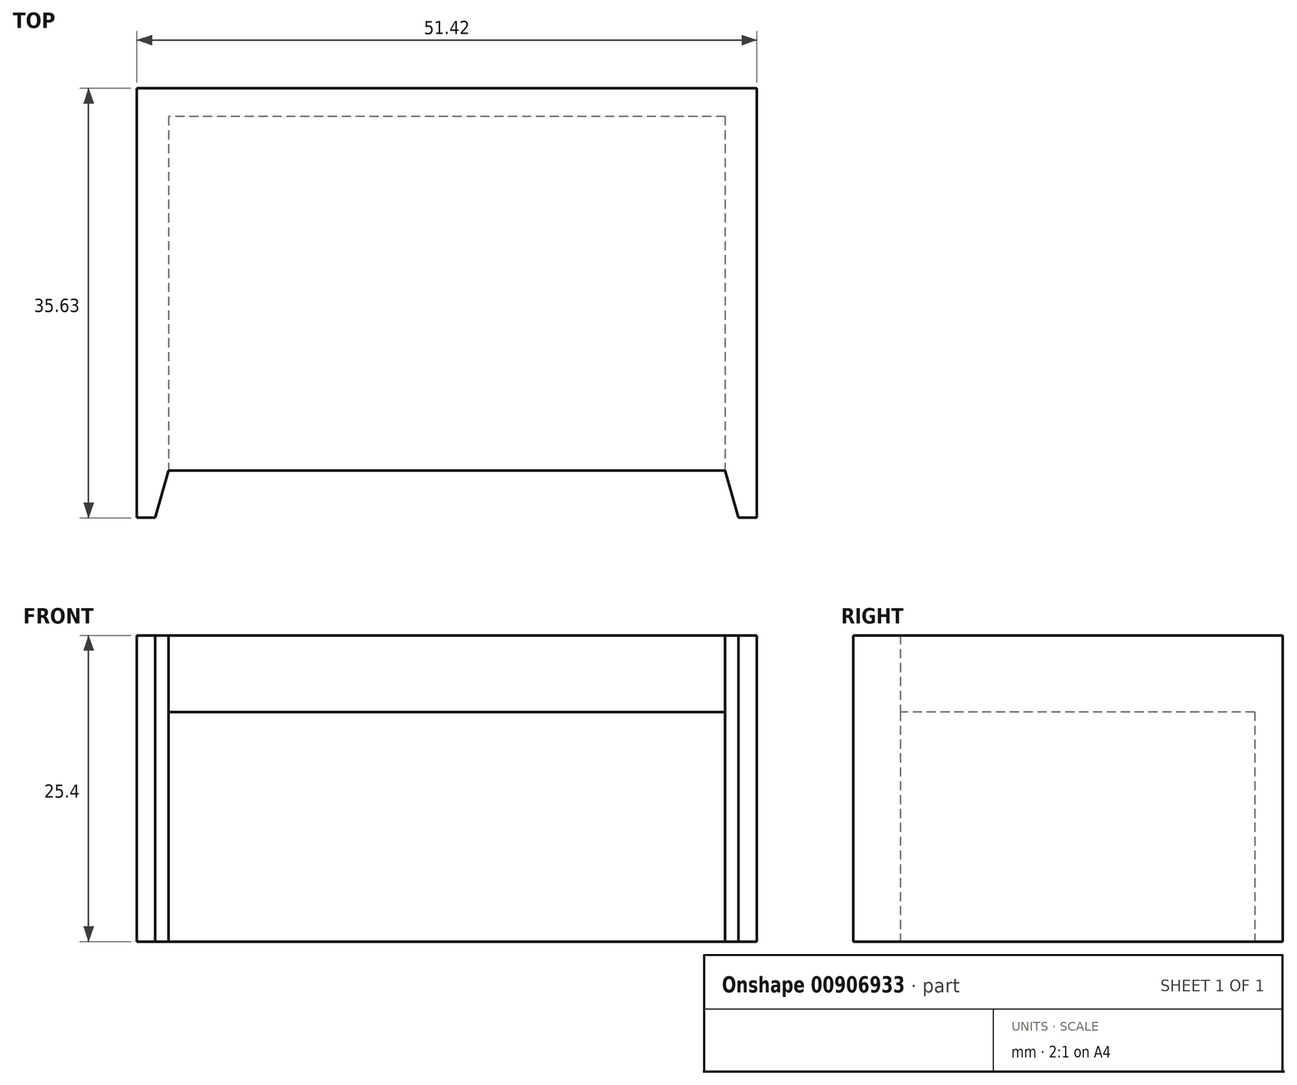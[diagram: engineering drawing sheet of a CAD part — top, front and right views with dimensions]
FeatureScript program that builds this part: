
annotation { "Feature Type Name" : "Feature", "Feature Type Description" : "" }
export const myFeature = defineFeature(function(context is Context, id is Id, definition is map)
    precondition{}
    {
        {
            var Q0;
            Q0=qCreatedBy(makeId("Top.planeOp"),FACE);
            var sketch = newSketch(context, id + "F0", { "sketchPlane" : qUnion([Q0])});
            skLineSegment(sketch, "E0.bottom", {"start": v(19.14, 62.7) * mm, "end": v(70.56, 62.7) * mm});
            skLineSegment(sketch, "E0.top", {"start": v(19.14, 31) * mm, "end": v(70.56, 31) * mm});
            skLineSegment(sketch, "E0.left", {"start": v(19.14, 62.7) * mm, "end": v(19.14, 31) * mm});
            skLineSegment(sketch, "E0.right", {"start": v(70.56, 62.7) * mm, "end": v(70.56, 31) * mm});
            skLineSegment(sketch, "E1.top", {"start": v(22.52, 31) * mm, "end": v(68.12, 31) * mm});
            skSolve(sketch);
        }
        {
            var Q0;
            Q0 = qSketchRegion(id + "F0", true);
            extrude(context, id + "F1", {"entities" : qUnion([Q0]), "depth" : 25.4 * mm, "offsetDistance" : 25.4 * mm});
        }
        {
            var Q0;
            Q0=makeQuery(id+"F1.opExtrude","CAP_FACE",FACE,{"disambiguationData":[OSD([sQuery(id+"F0.wireOp",EDGE,"E0.bottom"),sQuery(id+"F0.wireOp",EDGE,"E0.top"),sQuery(id+"F0.wireOp",EDGE,"E0.left"),sQuery(id+"F0.wireOp",EDGE,"E0.right"),sQuery(id+"F0.wireOp",EDGE,"E1.top")])],"isStart":true});
            var sketch = newSketch(context, id + "F2", { "sketchPlane" : qUnion([Q0])});
            skLineSegment(sketch, "E2.bottom", {"start": v(67.93, -60.38) * mm, "end": v(21.77, -60.38) * mm});
            skLineSegment(sketch, "E2.top", {"start": v(67.93, -31) * mm, "end": v(21.77, -31) * mm});
            skLineSegment(sketch, "E2.left", {"start": v(67.93, -60.38) * mm, "end": v(67.93, -31) * mm});
            skLineSegment(sketch, "E2.right", {"start": v(21.77, -60.38) * mm, "end": v(21.77, -31) * mm});
            skSolve(sketch);
        }
        {
            var Q0;
            Q0 = qSketchRegion(id + "F2", true);
            extrude(context, id + "F3", {"entities" : qUnion([Q0]), "operationType" : NewBodyOperationType.REMOVE, "oppositeDirection" : true, "depth" : 19.05 * mm, "offsetDistance" : 25.4 * mm});
        }
        {
            var Q0;
            Q0=makeQuery(id+"F1.opExtrude","CAP_FACE",FACE,{"disambiguationData":[OSD([sQuery(id+"F0.wireOp",EDGE,"E0.bottom"),sQuery(id+"F0.wireOp",EDGE,"E0.top"),sQuery(id+"F0.wireOp",EDGE,"E0.left"),sQuery(id+"F0.wireOp",EDGE,"E0.right"),sQuery(id+"F0.wireOp",EDGE,"E1.top")])],"isStart":true});
            var sketch = newSketch(context, id + "F4", { "sketchPlane" : qUnion([Q0])});
            skLineSegment(sketch, "E3", {"start": v(70.56, -31) * mm, "end": v(70.56, -27.08) * mm});
            skLineSegment(sketch, "E4", {"start": v(70.56, -27.08) * mm, "end": v(69.04, -27.08) * mm});
            skLineSegment(sketch, "E5", {"start": v(69.04, -27.08) * mm, "end": v(67.93, -31) * mm});
            skLineSegment(sketch, "E6", {"start": v(19.14, -31) * mm, "end": v(19.14, -27.08) * mm});
            skLineSegment(sketch, "E7", {"start": v(19.14, -27.08) * mm, "end": v(20.66, -27.08) * mm});
            skLineSegment(sketch, "E8", {"start": v(20.66, -27.08) * mm, "end": v(21.77, -31) * mm});
            skLineSegment(sketch, "E9", {"start": v(70.56, -27.08) * mm, "end": v(70.56, -24.91) * mm});
            skLineSegment(sketch, "E10", {"start": v(70.56, -24.91) * mm, "end": v(69.72, -23.49) * mm});
            skLineSegment(sketch, "E11", {"start": v(69.72, -23.49) * mm, "end": v(69.03, -24.91) * mm});
            skLineSegment(sketch, "E12", {"start": v(69.03, -24.91) * mm, "end": v(70.06, -25.7) * mm});
            skLineSegment(sketch, "E13", {"start": v(70.06, -25.7) * mm, "end": v(69.04, -27.08) * mm});
            skSolve(sketch);
        }
        {
            var Q0;
            Q0=makeQuery(id+"F4.imprint","IMPRINT",FACE,{"disambiguationData":[TD([[makeQuery(id+"F4.imprint","IMPRINT",EDGE,{"derivedFrom":sQuery(id+"F4.wireOp",EDGE,"E3")}),1.0]])]});
            var Q1;
            Q1=makeQuery(id+"F4.imprint","IMPRINT",FACE,{"disambiguationData":[TD([[makeQuery(id+"F4.imprint","IMPRINT",EDGE,{"derivedFrom":sQuery(id+"F4.wireOp",EDGE,"E6")}),-1.0]])]});
            extrude(context, id + "F5", {"entities" : qUnion([Q0, Q1]), "operationType" : NewBodyOperationType.ADD, "depth" : -25.4 * mm, "offsetDistance" : 25.4 * mm});
        }
    });
